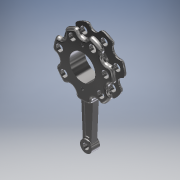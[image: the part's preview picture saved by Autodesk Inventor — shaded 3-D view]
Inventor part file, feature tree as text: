
AUTODESK INVENTOR PART (.ipt)
format: ipt  version: 2018 (Build 220112000, 112)  size: 571,392 bytes
history: native  units: mm
features: sketch x8, extrude x5, fillet x3, plane x1, hole x1, mirror x1
ambient origin geometry x8: Origin, YZ Plane, XZ Plane, XY Plane, X Axis, Y Axis, Z Axis, Center Point
bodies: Solid1 (feature_tree)
feature tree (19):
  extrude  "Extrusion1"  Depth=52.0mm
  sketch  "Sketch2"  dims[d2=41.96mm d3=10.0mm]
  plane  "Work Plane1"
  extrude  "Extrusion2"  Depth=10.0mm
  sketch  "Sketch4"  dims[d9=26.0mm d10=6.0mm]
  sketch  "Sketch5"  dims[d11=20.0mm d15=13.0mm d16=0.0mm d17=28.0mm]
  extrude  "Extrusion3"  Depth=70.0mm TaperAngle=360.0deg
  extrude  "Extrusion4"  Depth=6.0mm
  sketch  "Sketch6"  dims[d18=4.537856mm d19=34.0mm d20=4.537856mm d23=2.0mm]
  hole  "Hole1"  [1 undecoded]
  fillet  "Fillet1"  Radius=28.0mm
  extrude  "Extrusion6"  Depth=34.0mm
  mirror  "Mirror2"
  fillet  "Fillet2"  Radius=4.537856mm
  fillet  "Fillet3"  Radius=2.0mm
  sketch  "Sketch1"  dims[d0=22.0mm d1=52.0mm]
  sketch  "Sketch3"  dims[d4=5.74mm d5=70.0mm d7=360.0deg]
  sketch  "Sketch7"  dims[d26=7.0mm d27=0.0mm]
  sketch  "Sketch8"  dims[d28=60.0mm d29=5.0mm d30=10.0mm d31=9.96mm d32=7.23mm d33=1.93mm d34=1.5mm d36=1.93mm d37=0.94mm d38=0.94mm d39=0.94mm d40=7.0mm d41=0.0mm d42=5.0mm d43=0.0mm d46=16.0mm d47=16.0mm d48=2.459mm d49=6.0mm d50=4.0mm d51=2.0mm d52=90.0deg d53=16.55mm d54=20.594885mm d55=2.5mm d56=0.88mm d57=0.0mm d58=0.5mm d59=0.85mm]
note: 1 required parameter value undecoded (feature->parameter linkage not recoverable at this tier; creation-order binding heuristic only, values carry confidence <= 0.55)
